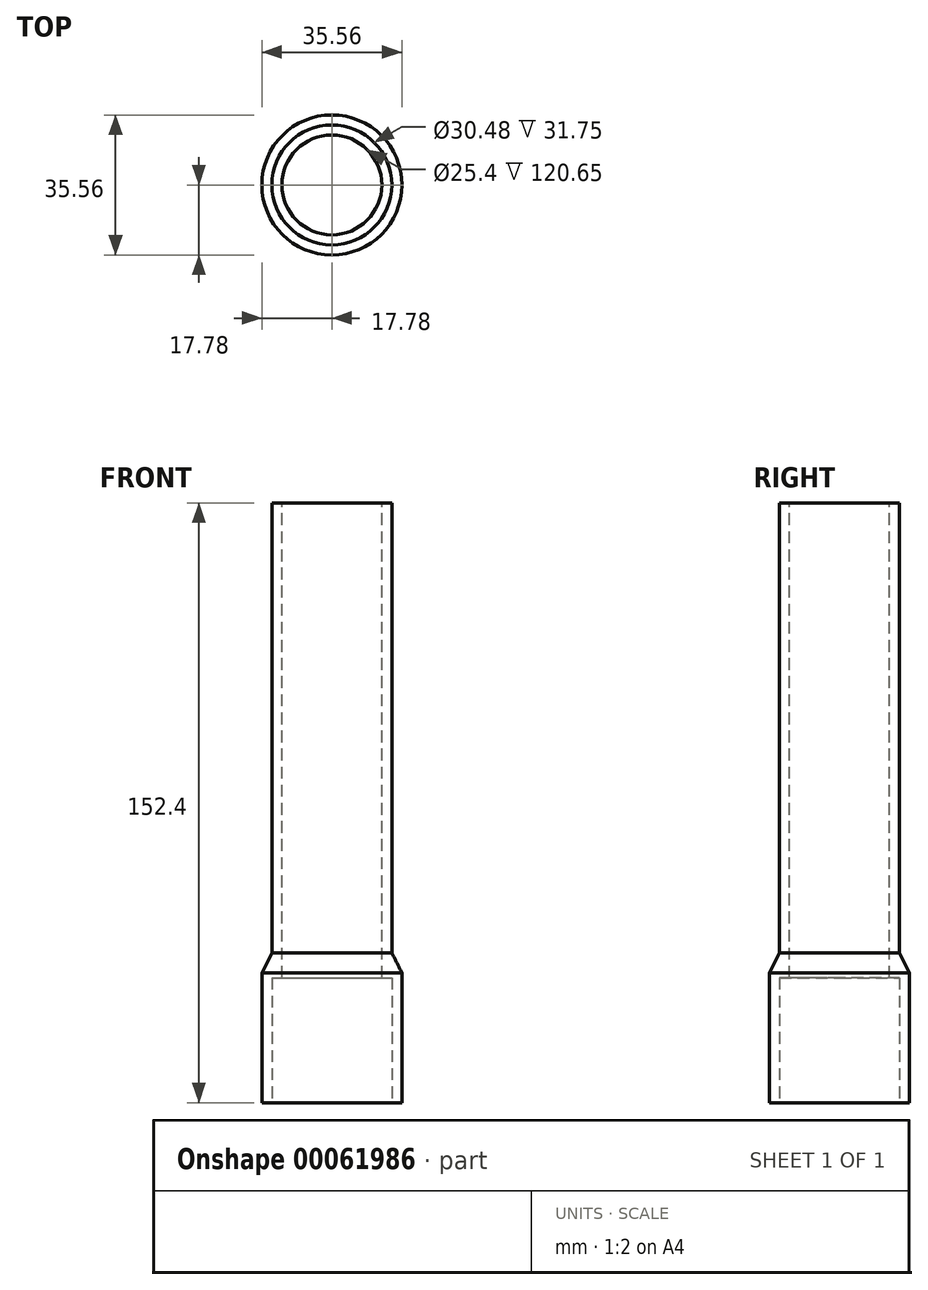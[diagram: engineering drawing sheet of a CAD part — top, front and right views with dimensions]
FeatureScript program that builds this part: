
annotation { "Feature Type Name" : "Feature", "Feature Type Description" : "" }
export const myFeature = defineFeature(function(context is Context, id is Id, definition is map)
    precondition{}
    {
        {
            var Q0;
            Q0=qCreatedBy(makeId("Top.planeOp"),FACE);
            var sketch = newSketch(context, id + "F0", { "sketchPlane" : qUnion([Q0])});
            skCircle(sketch, "E0", {"center": v(0, 0) * mm, "radius": 17.78 * mm});
            skSolve(sketch);
        }
        {
            var Q0;
            Q0 = qSketchRegion(id + "F0", true);
            extrude(context, id + "F1", {"entities" : qUnion([Q0]), "depth" : 38.1 * mm});
        }
        {
            var Q0;
            Q0=makeQuery(id+"F1.opExtrude","CAP_FACE",FACE,{"disambiguationData":[OSD([sQuery(id+"F0.wireOp",EDGE,"E0")])],"isStart":false});
            var sketch = newSketch(context, id + "F2", { "sketchPlane" : qUnion([Q0])});
            skCircle(sketch, "E1", {"center": v(0, 0) * mm, "radius": 15.24 * mm});
            skSolve(sketch);
        }
        {
            var Q0;
            Q0=makeQuery(id+"F2.imprint","IMPRINT",FACE,{"disambiguationData":[TD([[makeQuery(id+"F2.imprint","IMPRINT",EDGE,{"derivedFrom":sQuery(id+"F2.wireOp",EDGE,"E1")}),1.0]])]});
            extrude(context, id + "F3", {"entities" : qUnion([Q0]), "operationType" : NewBodyOperationType.ADD, "depth" : 114.3 * mm});
        }
        {
            var Q0;
            Q0=makeQuery(id+"F1.opExtrude","CAP_FACE",FACE,{"disambiguationData":[OSD([sQuery(id+"F0.wireOp",EDGE,"E0")])],"isStart":true});
            var sketch = newSketch(context, id + "F4", { "sketchPlane" : qUnion([Q0])});
            skCircle(sketch, "E2", {"center": v(0, 0) * mm, "radius": 15.24 * mm});
            skSolve(sketch);
        }
        {
            var Q0;
            Q0 = qSketchRegion(id + "F4", true);
            extrude(context, id + "F5", {"entities" : qUnion([Q0]), "operationType" : NewBodyOperationType.REMOVE, "oppositeDirection" : true, "depth" : 31.75 * mm});
        }
        {
            var Q0;
            Q0=makeQuery(id+"F3.opExtrude","CAP_FACE",FACE,{"disambiguationData":[OSD([sQuery(id+"F2.wireOp",EDGE,"E1")])],"isStart":false});
            var sketch = newSketch(context, id + "F6", { "sketchPlane" : qUnion([Q0])});
            skCircle(sketch, "E3", {"center": v(0, 0) * mm, "radius": 12.7 * mm});
            skSolve(sketch);
        }
        {
            var Q0;
            Q0 = qSketchRegion(id + "F6", true);
            extrude(context, id + "F7", {"entities" : qUnion([Q0]), "operationType" : NewBodyOperationType.REMOVE, "oppositeDirection" : true, "depth" : 127 * mm});
        }
        {
            var Q0;
            Q0=makeQuery(id+"F1.opExtrude","CAP_EDGE",EDGE,{"disambiguationData":[OSD([sQuery(id+"F0.wireOp",EDGE,"E0")])],"isStart":false});
            chamfer(context, id + "F8", {"entities" : qUnion([Q0]), "chamferType" : ChamferType.TWO_OFFSETS, "width1" : 2.54 * mm, "oppositeDirection" : false, "width2" : 5.08 * mm, "tangentPropagation" : true});
        }
    });
